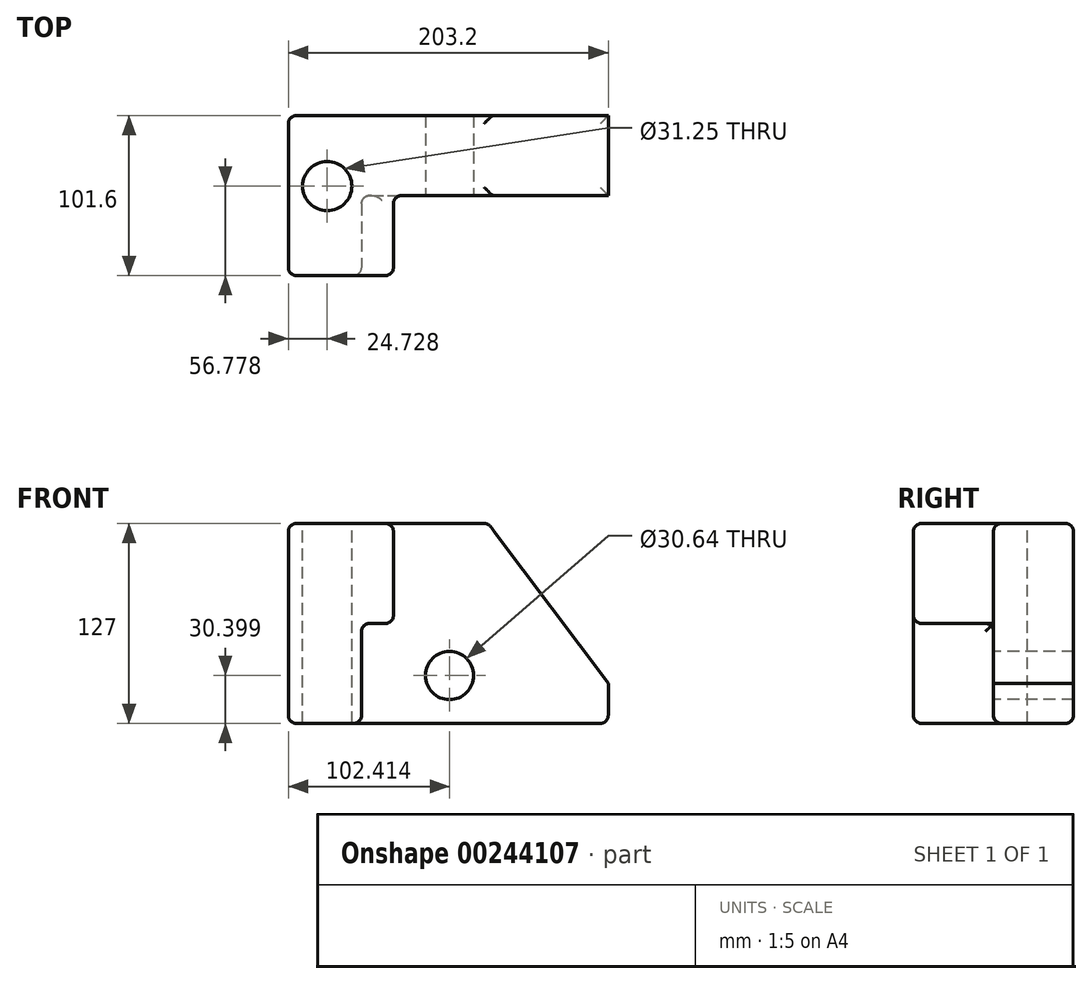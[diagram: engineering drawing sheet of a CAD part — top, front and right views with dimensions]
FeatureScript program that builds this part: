
annotation { "Feature Type Name" : "Feature", "Feature Type Description" : "" }
export const myFeature = defineFeature(function(context is Context, id is Id, definition is map)
    precondition{}
    {
        {
            var Q0;
            Q0=qCreatedBy(makeId("Front.planeOp"),FACE);
            var sketch = newSketch(context, id + "F0", { "sketchPlane" : qUnion([Q0])});
            skLineSegment(sketch, "E0.bottom", {"start": v(-101.6, 63.5) * mm, "end": v(101.6, 63.5) * mm});
            skLineSegment(sketch, "E0.top", {"start": v(-101.6, -63.5) * mm, "end": v(101.6, -63.5) * mm});
            skLineSegment(sketch, "E0.left", {"start": v(-101.6, 63.5) * mm, "end": v(-101.6, -63.5) * mm});
            skLineSegment(sketch, "E0.right", {"start": v(101.6, 63.5) * mm, "end": v(101.6, -63.5) * mm});
            skPoint(sketch, "E0.middle", {"position": v(0, 0) * mm});
            skSolve(sketch);
        }
        {
            var Q0;
            Q0=makeQuery(id+"F0.imprint","IMPRINT",FACE,{"disambiguationData":[TD([[makeQuery(id+"F0.imprint","IMPRINT",EDGE,{"derivedFrom":sQuery(id+"F0.wireOp",EDGE,"E0.bottom")}),-1.0]])]});
            extrude(context, id + "F1", {"entities" : qUnion([Q0]), "depth" : 101.6 * mm});
        }
        {
            var Q0;
            Q0=makeQuery(id+"F1.opExtrude","CAP_FACE",FACE,{"disambiguationData":[OSD([sQuery(id+"F0.wireOp",EDGE,"E0.bottom"),sQuery(id+"F0.wireOp",EDGE,"E0.top"),sQuery(id+"F0.wireOp",EDGE,"E0.left"),sQuery(id+"F0.wireOp",EDGE,"E0.right")])],"isStart":false});
            var sketch = newSketch(context, id + "F2", { "sketchPlane" : qUnion([Q0])});
            skLineSegment(sketch, "E1", {"start": v(-34.83, 63.5) * mm, "end": v(-34.83, 0) * mm});
            skLineSegment(sketch, "E2", {"start": v(-34.83, 0) * mm, "end": v(-55.07, 0) * mm});
            skLineSegment(sketch, "E3", {"start": v(-55.07, 0) * mm, "end": v(-55.07, -63.5) * mm});
            skLineSegment(sketch, "E4", {"start": v(-55.07, -63.5) * mm, "end": v(-101.6, -63.5) * mm});
            skLineSegment(sketch, "E5", {"start": v(-101.6, -63.5) * mm, "end": v(-101.6, 63.5) * mm});
            skLineSegment(sketch, "E6", {"start": v(-101.6, 63.5) * mm, "end": v(-34.83, 63.5) * mm});
            skSolve(sketch);
        }
        {
            var Q0;
            {var subQ2=sQuery(id+"F2.wireOp",EDGE,"E1");Q0=makeQuery(id+"F2.imprint","IMPRINT",FACE,{"disambiguationData":[TD([[makeQuery(id+"F2.imprint","IMPRINT",EDGE,{"derivedFrom":subQ2}),1.0]])]});}
            extrude(context, id + "F3", {"entities" : qUnion([Q0]), "operationType" : NewBodyOperationType.REMOVE, "oppositeDirection" : true, "depth" : 50.8 * mm});
        }
        {
            var Q0;
            Q0=makeQuery(id+"F1.opExtrude","SWEPT_EDGE",EDGE,{"disambiguationData":[OSD([sQuery(id+"F0.wireOp",EDGE,"E0.bottom"),sQuery(id+"F0.wireOp",EDGE,"E0.right")])]});
            chamfer(context, id + "F4", {"entities" : qUnion([Q0]), "chamferType" : ChamferType.TWO_OFFSETS, "width1" : 76.2 * mm, "oppositeDirection" : false, "width2" : 101.6 * mm, "tangentPropagation" : true});
        }
        {
            var Q0;
            Q0=makeQuery(id+"F1.opExtrude","SWEPT_FACE",FACE,{"disambiguationData":[OSD([sQuery(id+"F0.wireOp",EDGE,"E0.bottom")])]});
            var Q1;
            Q1=makeQuery(id+"F3.boolean.opBoolean","COPY",FACE,{"derivedFrom":makeQuery(id+"F3.opExtrude","SWEPT_FACE",FACE,{"disambiguationData":[OSD([sQuery(id+"F2.wireOp",EDGE,"E1")])]})});
            var Q2;
            Q2=makeQuery(id+"F3.boolean.opBoolean","COPY",FACE,{"derivedFrom":makeQuery(id+"F3.opExtrude","SWEPT_FACE",FACE,{"disambiguationData":[OSD([sQuery(id+"F2.wireOp",EDGE,"E3")])]})});
            var Q3;
            Q3=makeQuery(id+"F1.opExtrude","CAP_FACE",FACE,{"disambiguationData":[OSD([sQuery(id+"F0.wireOp",EDGE,"E0.bottom"),sQuery(id+"F0.wireOp",EDGE,"E0.top"),sQuery(id+"F0.wireOp",EDGE,"E0.left"),sQuery(id+"F0.wireOp",EDGE,"E0.right")])],"isStart":false});
            var Q4;
            Q4=makeQuery(id+"F3.boolean.opBoolean","COPY",EDGE,{"derivedFrom":makeQuery(id+"F3.opExtrude","CAP_EDGE",EDGE,{"disambiguationData":[OSD([sQuery(id+"F0.wireOp",EDGE,"E0.top")])],"isStart":false})});
            var Q5;
            Q5=makeQuery(id+"F1.opExtrude","CAP_EDGE",EDGE,{"disambiguationData":[OSD([sQuery(id+"F0.wireOp",EDGE,"E0.left")])],"isStart":true});
            var Q6;
            Q6=makeQuery(id+"F1.opExtrude","CAP_EDGE",EDGE,{"disambiguationData":[OSD([sQuery(id+"F0.wireOp",EDGE,"E0.top")])],"isStart":true});
            var Q7;
            Q7=makeQuery(id+"F1.opExtrude","SWEPT_EDGE",EDGE,{"disambiguationData":[OSD([sQuery(id+"F0.wireOp",EDGE,"E0.top"),sQuery(id+"F0.wireOp",EDGE,"E0.left")])]});
            var Q8;
            Q8=makeQuery(id+"F1.opExtrude","SWEPT_FACE",FACE,{"disambiguationData":[OSD([sQuery(id+"F0.wireOp",EDGE,"E0.top")])]});
            fillet(context, id + "F5", {"entities" : qUnion([Q0, Q1, Q2, Q3, Q4, Q5, Q6, Q7, Q8]), "radius" : 5.08 * mm, "tangentPropagation" : true, "allowEdgeOverflow" : false});
        }
        {
            var Q0;
            Q0=makeQuery(id+"F3.boolean.opBoolean","COPY",FACE,{"derivedFrom":makeQuery(id+"F3.opExtrude","CAP_FACE",FACE,{"disambiguationData":[OSD([sQuery(id+"F0.wireOp",EDGE,"E0.bottom"),sQuery(id+"F0.wireOp",EDGE,"E0.top"),sQuery(id+"F0.wireOp",EDGE,"E0.right"),sQuery(id+"F2.wireOp",EDGE,"E1"),sQuery(id+"F2.wireOp",EDGE,"E2"),sQuery(id+"F2.wireOp",EDGE,"E3")])],"isStart":false})});
            var sketch = newSketch(context, id + "F6", { "sketchPlane" : qUnion([Q0])});
            skCircle(sketch, "E7", {"center": v(0.81, -33.1) * mm, "radius": 15.32 * mm});
            skSolve(sketch);
        }
        {
            var Q0;
            Q0=makeQuery(id+"F6.imprint","IMPRINT",FACE,{"disambiguationData":[TD([[makeQuery(id+"F6.imprint","IMPRINT",EDGE,{"derivedFrom":sQuery(id+"F6.wireOp",EDGE,"E7")}),1.0]])]});
            extrude(context, id + "F7", {"entities" : qUnion([Q0]), "operationType" : NewBodyOperationType.REMOVE, "endBound" : BoundingType.UP_TO_NEXT, "oppositeDirection" : true, "depth" : 25.4 * mm});
        }
        {
            var Q0;
            Q0=makeQuery(id+"F1.opExtrude","SWEPT_FACE",FACE,{"disambiguationData":[OSD([sQuery(id+"F0.wireOp",EDGE,"E0.bottom")])]});
            var sketch = newSketch(context, id + "F8", { "sketchPlane" : qUnion([Q0])});
            skCircle(sketch, "E8", {"center": v(-76.87, -44.82) * mm, "radius": 15.63 * mm});
            skSolve(sketch);
        }
        {
            var Q0;
            Q0=makeQuery(id+"F8.imprint","IMPRINT",FACE,{"disambiguationData":[TD([[makeQuery(id+"F8.imprint","IMPRINT",EDGE,{"derivedFrom":sQuery(id+"F8.wireOp",EDGE,"E8")}),1.0]])]});
            extrude(context, id + "F9", {"entities" : qUnion([Q0]), "operationType" : NewBodyOperationType.REMOVE, "endBound" : BoundingType.UP_TO_NEXT, "oppositeDirection" : true, "depth" : 25.4 * mm});
        }
    });
